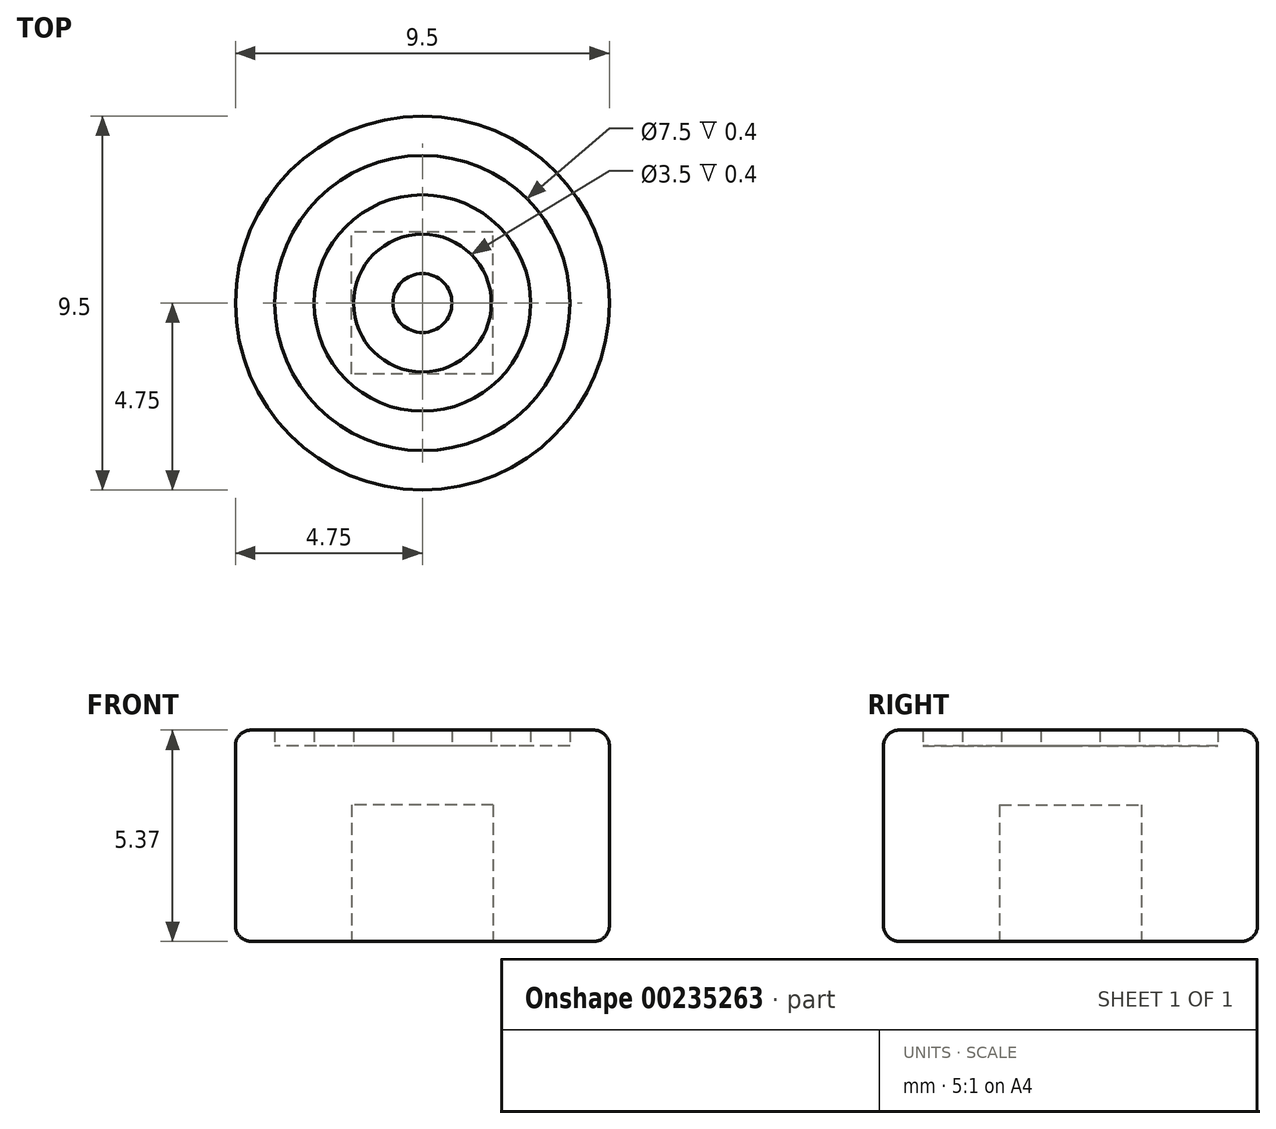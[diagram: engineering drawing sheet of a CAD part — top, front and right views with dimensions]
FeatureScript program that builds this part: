
annotation { "Feature Type Name" : "Feature", "Feature Type Description" : "" }
export const myFeature = defineFeature(function(context is Context, id is Id, definition is map)
    precondition{}
    {
        {
            var Q0;
            Q0=qCreatedBy(makeId("Top.planeOp"),FACE);
            var sketch = newSketch(context, id + "F0", { "sketchPlane" : qUnion([Q0])});
            skLineSegment(sketch, "E0.bottom", {"start": v(1.8, -1.8) * mm, "end": v(-1.8, -1.8) * mm});
            skLineSegment(sketch, "E0.top", {"start": v(1.8, 1.8) * mm, "end": v(-1.8, 1.8) * mm});
            skLineSegment(sketch, "E0.left", {"start": v(1.8, -1.8) * mm, "end": v(1.8, 1.8) * mm});
            skLineSegment(sketch, "E0.right", {"start": v(-1.8, -1.8) * mm, "end": v(-1.8, 1.8) * mm});
            skPoint(sketch, "E0.middle", {"position": v(0, 0) * mm});
            skCircle(sketch, "E1", {"center": v(0, 0) * mm, "radius": 4.75 * mm});
            skSolve(sketch);
        }
        {
            var Q0;
            Q0=makeQuery(id+"F0.imprint","IMPRINT",FACE,{"disambiguationData":[TD([[makeQuery(id+"F0.imprint","IMPRINT",EDGE,{"derivedFrom":sQuery(id+"F0.wireOp",EDGE,"E0.bottom")}),1.0]])]});
            extrude(context, id + "F1", {"entities" : qUnion([Q0]), "depth" : 3.47 * mm});
        }
        {
            var Q0;
            Q0=makeQuery(id+"F1.opExtrude","CAP_FACE",FACE,{"disambiguationData":[OSD([sQuery(id+"F0.wireOp",EDGE,"E0.bottom"),sQuery(id+"F0.wireOp",EDGE,"E0.top"),sQuery(id+"F0.wireOp",EDGE,"E0.left"),sQuery(id+"F0.wireOp",EDGE,"E0.right"),sQuery(id+"F0.wireOp",EDGE,"E1")])],"isStart":false});
            var sketch = newSketch(context, id + "F2", { "sketchPlane" : qUnion([Q0])});
            skSolve(sketch);
        }
        {
            var Q0;
            Q0 = qSketchRegion(id + "F2", true);
            var Q1;
            Q1=makeQuery(id+"F2.imprint","IMPRINT",FACE,{"disambiguationData":[TD([[makeQuery(id+"F2.imprint","IMPRINT",EDGE,{"derivedFrom":makeQuery(id+"F1.opExtrude","CAP_EDGE",EDGE,{"disambiguationData":[OSD([sQuery(id+"F0.wireOp",EDGE,"E0.bottom")])],"isStart":false})}),1.0]])]});
            var Q2;
            Q2=makeQuery(id+"F2.imprint","IMPRINT",FACE,{"disambiguationData":[TD([[makeQuery(id+"F2.imprint","IMPRINT",EDGE,{"derivedFrom":makeQuery(id+"F1.opExtrude","CAP_EDGE",EDGE,{"disambiguationData":[OSD([sQuery(id+"F0.wireOp",EDGE,"E0.bottom")])],"isStart":false})}),-1.0]])]});
            extrude(context, id + "F3", {"entities" : qUnion([Q0, Q1, Q2]), "operationType" : NewBodyOperationType.ADD, "depth" : 1.5 * mm});
        }
        {
            var Q0;
            Q0=makeQuery(id+"F3.opExtrude","CAP_FACE",FACE,{"disambiguationData":[OSD([sQuery(id+"F0.wireOp",EDGE,"E1")])],"isStart":false});
            var sketch = newSketch(context, id + "F4", { "sketchPlane" : qUnion([Q0])});
            skCircle(sketch, "E2", {"center": v(0, 0) * mm, "radius": 3.75 * mm});
            skCircle(sketch, "E3", {"center": v(0, 0) * mm, "radius": 2.75 * mm});
            skCircle(sketch, "E4", {"center": v(0, 0) * mm, "radius": 1.75 * mm});
            skCircle(sketch, "E5", {"center": v(0, 0) * mm, "radius": 0.75 * mm});
            skSolve(sketch);
        }
        {
            var Q0;
            Q0=makeQuery(id+"F4.imprint","IMPRINT",FACE,{"disambiguationData":[TD([[makeQuery(id+"F4.imprint","IMPRINT",EDGE,{"derivedFrom":sQuery(id+"F4.wireOp",EDGE,"E2")}),-1.0]])]});
            var Q1;
            Q1=makeQuery(id+"F4.imprint","IMPRINT",FACE,{"disambiguationData":[TD([[makeQuery(id+"F4.imprint","IMPRINT",EDGE,{"derivedFrom":sQuery(id+"F4.wireOp",EDGE,"E3")}),1.0]])]});
            var Q2;
            Q2=makeQuery(id+"F4.imprint","IMPRINT",FACE,{"disambiguationData":[TD([[makeQuery(id+"F4.imprint","IMPRINT",EDGE,{"derivedFrom":sQuery(id+"F4.wireOp",EDGE,"E5")}),1.0]])]});
            extrude(context, id + "F5", {"entities" : qUnion([Q0, Q1, Q2]), "operationType" : NewBodyOperationType.ADD, "depth" : .4 * mm});
        }
        {
            var Q0;
            Q0=makeQuery(id+"F5.opExtrude","CAP_EDGE",EDGE,{"disambiguationData":[OSD([sQuery(id+"F0.wireOp",EDGE,"E1")])],"isStart":false});
            var Q1;
            Q1=makeQuery(id+"F1.opExtrude","CAP_EDGE",EDGE,{"disambiguationData":[OSD([sQuery(id+"F0.wireOp",EDGE,"E1")])],"isStart":true});
            fillet(context, id + "F6", {"entities" : qUnion([Q0, Q1]), "radius" : 0.4 * mm, "tangentPropagation" : true, "allowEdgeOverflow" : false});
        }
    });
